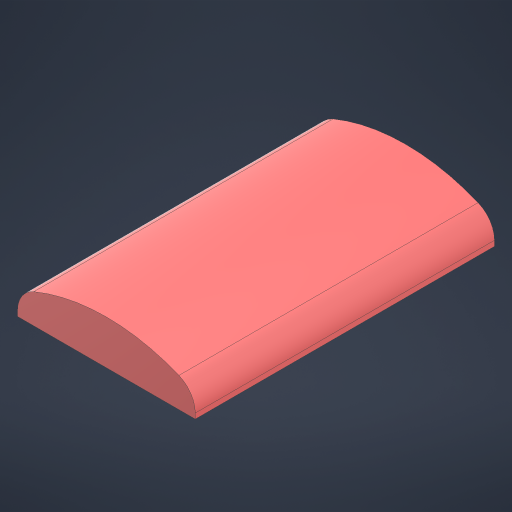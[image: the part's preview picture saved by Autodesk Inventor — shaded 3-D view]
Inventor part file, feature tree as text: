
AUTODESK INVENTOR PART (.ipt)
format: ipt  version: 2023 (Build 270158030, 158C)  size: 186,368 bytes
history: native  units: in
note: dims shown in document units (in); Inventor stores cm internally (conversion verified against a paired STEP export)
features: extrude x2, sketch x2, fillet x1
ambient origin geometry x8: Origin, YZ Plane, XZ Plane, XY Plane, X Axis, Y Axis, Z Axis, Center Point
bodies: Solid1 (feature_tree)
feature tree (5):
  extrude  "Extrusion1"  Depth=0.6693in
  extrude  "Extrusion2"  Depth=0.0591in TaperAngle=0.0deg
  fillet  "Fillet1"  Radius=0.0591in
  sketch  "Sketch1"  dims[d0=0.3976in d1=0.6693in]
  sketch  "Sketch2"  dims[d2=0.0984in d3=0.0in d4=0.7141in d5=0.0in d6=0.0591in]
